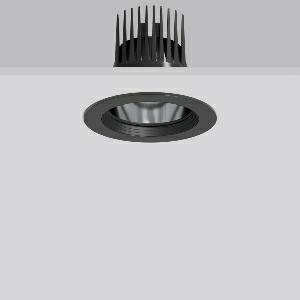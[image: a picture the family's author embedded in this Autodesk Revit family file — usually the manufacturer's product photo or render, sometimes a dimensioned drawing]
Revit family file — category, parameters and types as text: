
# Revit family: heledon_maxi_e_901759_003_76_953a
name_source: partatom
category: Lighting Fixtures
units: mm (PartAtom-declared; Revit-internal decimal feet)

## family parameters
Cut with Voids When Loaded = No
Host = Face
Light Source = No
Part Type = Normal
Room Calculation Point = No
Round Connector Dimension = Use Diameter
Shared = No

## types (1)
- HELEDON maxi E (1 x LED Modul 930, 3250 lm, 3000)
    Apparent Load = 25 VA
    Approval mark = CE
    CIE Flux Codes = 97 100 100 100 100
    Color Rendering = 90
    Color Temperature = 3000
    Default Elevation = 1800 mm
    Description = Series: HELEDON maxi
Round recessed downlight. Housing: die-cast aluminium, powder-coated. Black plastic ring and recessed LED to prevent glare from the side. Optical assembly with reflector made of MIRO-Silver with 98% total light reflection for outstanding efficiency - can be changed without tools. Best colour rendering index Ra>90. Suitable for Recessed ceiling mounting. Installation without tools thanks to spring fastening system. Including separate LED converter with connecting cable 600 mm.High quality converter without flickering and stroboscopic effect. Through-wiring box (5 pole) available as accessory. The following accessories can be mounted without use of tools: interchangeable lenses, decorative glasses, honeycomb louvre, clear and frosted diffusers, white interchangeable plastic ring. 
Colour: deep black, matt (RAL 9005)
Diameter: 162 mm
Height: 3 mm
Cut-out diameter: 152 mm
Recess height: 200 mm
Luminaire: recess height: 135 mm
Lamp: LED
Socket: without socket
Colour temperature: 3000K
Colour rendering index (CRI): 92
System power: 25 W
Rated luminous flux: 3250 lm
Luminous efficiency: 130 lm/W
Control gear: Converter, dimmable, DALI
Protection class: II
Type of protection: IP 20
    Height = 0 mm  [stored 0 ft]
    Lamp = 1 x LED Modul 930
    Lamp Light Flux = 3250 lm
    Lamp count = 1
    Length = 162 mm
    Lifetime = 50000 h
    Luminous efficacy = 130 lm/W
    Manufacturer = RZB
    ModVariant = No
    Model = 901759.003.76
    Mounting Place = Ceiling
    Mounting Type = Recessed
    Number of Poles = 1
    OnlyDefault = Yes
    Power Factor = 1
    Product Name = HELEDON maxi E
    Product group = Recessed downlights
    ProductGroupID = 402
    Protection Class = Protection class II
    Protection Degree = IP 20
    RLX_Detail_Level = 1
    RLX_Emergency_Light_Flux = 0 lm
    RLX_Emergency_Type = 0
    RLX_Emergency_Type_DB = No
    RlxData = <blob elided: 123805 chars, md5=7fe2eb33>
    Socket = socket
    Standby Power = 0 W
    System Light Flux = 3250 lm
    System Power = 25 W
    Type Comments = Product without accessories
    Type Image = 901662.003.jpg
    URL = http://relux.com
    VarID = ---
    Voltage = 230 V
    Voltage Range = 220-240 V
    Weight = 0.00 kg
    Width = 0 mm  [stored 0 ft]

note: [stored X ft] marks values corroborated as IEEE doubles in the binary element streams (Revit-internal decimal feet)

## geometry (parser evidence)
native form markers: Blend x4, Sweep x10
no freeform markers — native parametric forms only
